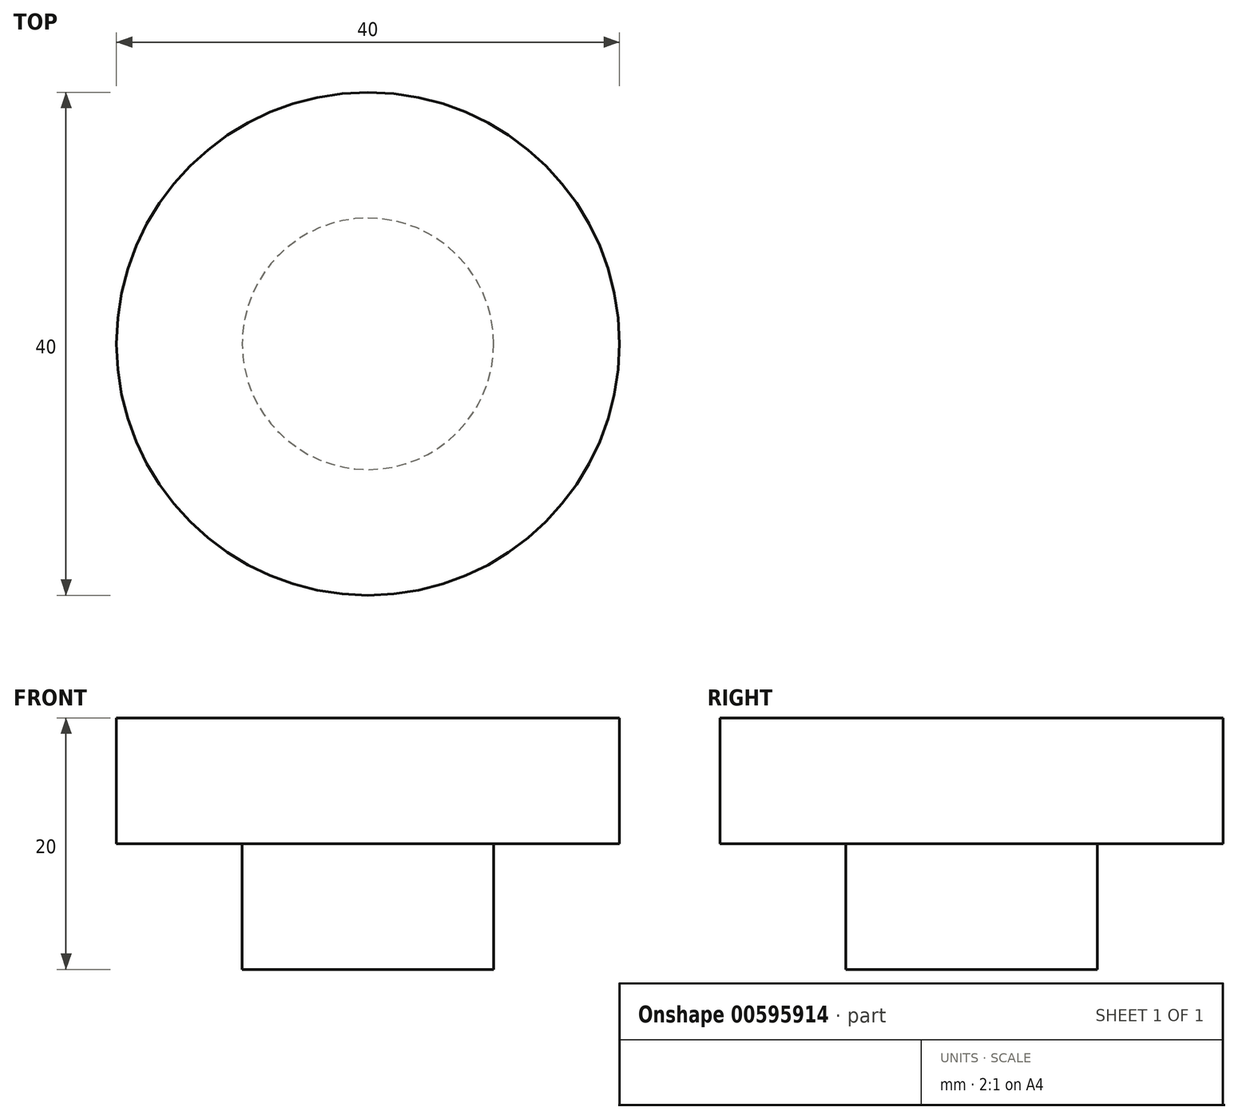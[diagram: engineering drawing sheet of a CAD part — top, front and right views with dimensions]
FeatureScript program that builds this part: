
annotation { "Feature Type Name" : "Feature", "Feature Type Description" : "" }
export const myFeature = defineFeature(function(context is Context, id is Id, definition is map)
    precondition{}
    {
        {
            var Q0;
            Q0=qCreatedBy(makeId("Top.planeOp"),FACE);
            var sketch = newSketch(context, id + "F0", { "sketchPlane" : qUnion([Q0])});
            skCircle(sketch, "E0", {"center": v(0, 0) * mm, "radius": 10 * mm});
            skSolve(sketch);
        }
        {
            var Q0;
            Q0=makeQuery(id+"F0.imprint","IMPRINT",FACE,{"disambiguationData":[TD([[makeQuery(id+"F0.imprint","IMPRINT",EDGE,{"derivedFrom":sQuery(id+"F0.wireOp",EDGE,"E0")}),1.0]])]});
            extrude(context, id + "F1", {"entities" : qUnion([Q0]), "depth" : 10 * mm, "offsetDistance" : 25 * mm});
        }
        {
            var Q0;
            Q0=makeQuery(id+"F1.opExtrude","CAP_FACE",FACE,{"disambiguationData":[OSD([sQuery(id+"F0.wireOp",EDGE,"E0")])],"isStart":false});
            var sketch = newSketch(context, id + "F2", { "sketchPlane" : qUnion([Q0])});
            skCircle(sketch, "E1", {"center": v(0, 0) * mm, "radius": 20 * mm});
            skSolve(sketch);
        }
        {
            var Q0;
            Q0=makeQuery(id+"F2.imprint","IMPRINT",FACE,{"disambiguationData":[TD([[makeQuery(id+"F2.imprint","IMPRINT",EDGE,{"derivedFrom":makeQuery(id+"F1.opExtrude","CAP_EDGE",EDGE,{"disambiguationData":[OSD([sQuery(id+"F0.wireOp",EDGE,"E0")])],"isStart":false})}),1.0]])]});
            var Q1;
            Q1=makeQuery(id+"F2.imprint","IMPRINT",FACE,{"disambiguationData":[TD([[makeQuery(id+"F2.imprint","IMPRINT",EDGE,{"derivedFrom":sQuery(id+"F2.wireOp",EDGE,"E1")}),1.0]])]});
            extrude(context, id + "F3", {"entities" : qUnion([Q0, Q1]), "operationType" : NewBodyOperationType.ADD, "depth" : 10 * mm, "offsetDistance" : 25 * mm});
        }
    });
